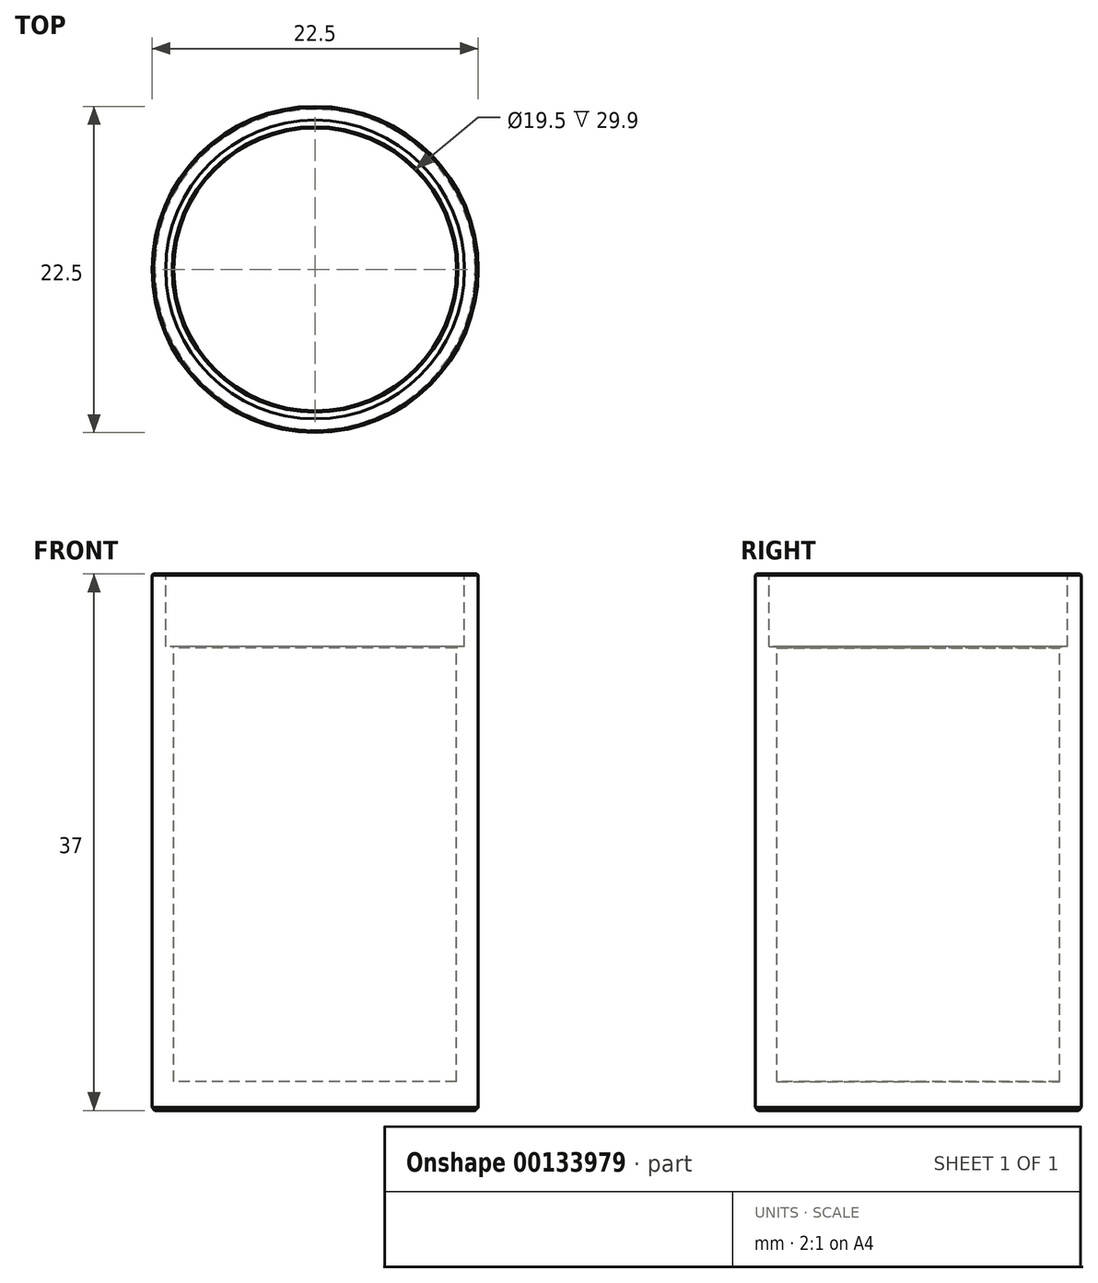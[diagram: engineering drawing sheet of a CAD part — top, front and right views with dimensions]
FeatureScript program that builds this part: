
annotation { "Feature Type Name" : "Feature", "Feature Type Description" : "" }
export const myFeature = defineFeature(function(context is Context, id is Id, definition is map)
    precondition{}
    {
        {
            var Q0;
            Q0=qCreatedBy(makeId("Top.planeOp"),FACE);
            var sketch = newSketch(context, id + "F0", { "sketchPlane" : qUnion([Q0])});
            skCircle(sketch, "E0", {"center": v(0, 0) * mm, "radius": 11.25 * mm});
            skSolve(sketch);
        }
        {
            var Q0;
            Q0 = qSketchRegion(id + "F0", true);
            extrude(context, id + "F1", {"entities" : qUnion([Q0]), "depth" : 37 * mm, "offsetDistance" : 25 * mm});
        }
        {
            var Q0;
            Q0=makeQuery(id+"F1.opExtrude","CAP_FACE",FACE,{"disambiguationData":[OSD([sQuery(id+"F0.wireOp",EDGE,"E0")])],"isStart":false});
            var sketch = newSketch(context, id + "F2", { "sketchPlane" : qUnion([Q0])});
            skCircle(sketch, "E1", {"center": v(0, 0) * mm, "radius": 9.75 * mm});
            skSolve(sketch);
        }
        {
            var Q0;
            Q0 = qSketchRegion(id + "F2", true);
            extrude(context, id + "F3", {"entities" : qUnion([Q0]), "operationType" : NewBodyOperationType.REMOVE, "oppositeDirection" : true, "depth" : 35 * mm, "offsetDistance" : 25 * mm});
        }
        {
            var Q0;
            Q0=makeQuery(id+"F1.opExtrude","CAP_FACE",FACE,{"disambiguationData":[OSD([sQuery(id+"F0.wireOp",EDGE,"E0")])],"isStart":false});
            var sketch = newSketch(context, id + "F4", { "sketchPlane" : qUnion([Q0])});
            skCircle(sketch, "E2", {"center": v(0, 0) * mm, "radius": 10.3 * mm});
            skSolve(sketch);
        }
        {
            var Q0;
            Q0 = qSketchRegion(id + "F4", true);
            extrude(context, id + "F5", {"entities" : qUnion([Q0]), "operationType" : NewBodyOperationType.REMOVE, "oppositeDirection" : true, "depth" : 5 * mm, "offsetDistance" : 25 * mm});
        }
        {
            var Q0;
            Q0=makeQuery(id+"F5.boolean.opBoolean","COPY",EDGE,{"derivedFrom":makeQuery(id+"F5.opExtrude","CAP_EDGE",EDGE,{"disambiguationData":[OSD([sQuery(id+"F4.wireOp",EDGE,"E2")])],"isStart":true})});
            var Q1;
            Q1=makeQuery(id+"F1.opExtrude","CAP_EDGE",EDGE,{"disambiguationData":[OSD([sQuery(id+"F0.wireOp",EDGE,"E0")])],"isStart":false});
            var Q2;
            Q2=makeQuery(id+"F5.boolean.opBoolean","INTERSECT",EDGE,{"derivedFrom":[makeQuery(id+"F3.boolean.opBoolean","COPY",FACE,{"derivedFrom":makeQuery(id+"F3.opExtrude","SWEPT_FACE",FACE,{"disambiguationData":[OSD([sQuery(id+"F2.wireOp",EDGE,"E1")])]})}),makeQuery(id+"F5.opExtrude","CAP_FACE",FACE,{"disambiguationData":[OSD([sQuery(id+"F4.wireOp",EDGE,"E2")])],"isStart":false})]});
            chamfer(context, id + "F6", {"entities" : qUnion([Q0, Q1, Q2]), "width" : 0.1 * mm, "tangentPropagation" : true});
        }
        {
            var Q0;
            Q0=makeQuery(id+"F1.opExtrude","CAP_EDGE",EDGE,{"disambiguationData":[OSD([sQuery(id+"F0.wireOp",EDGE,"E0")])],"isStart":true});
            chamfer(context, id + "F7", {"entities" : qUnion([Q0]), "width" : 0.2 * mm, "tangentPropagation" : true});
        }
    });
